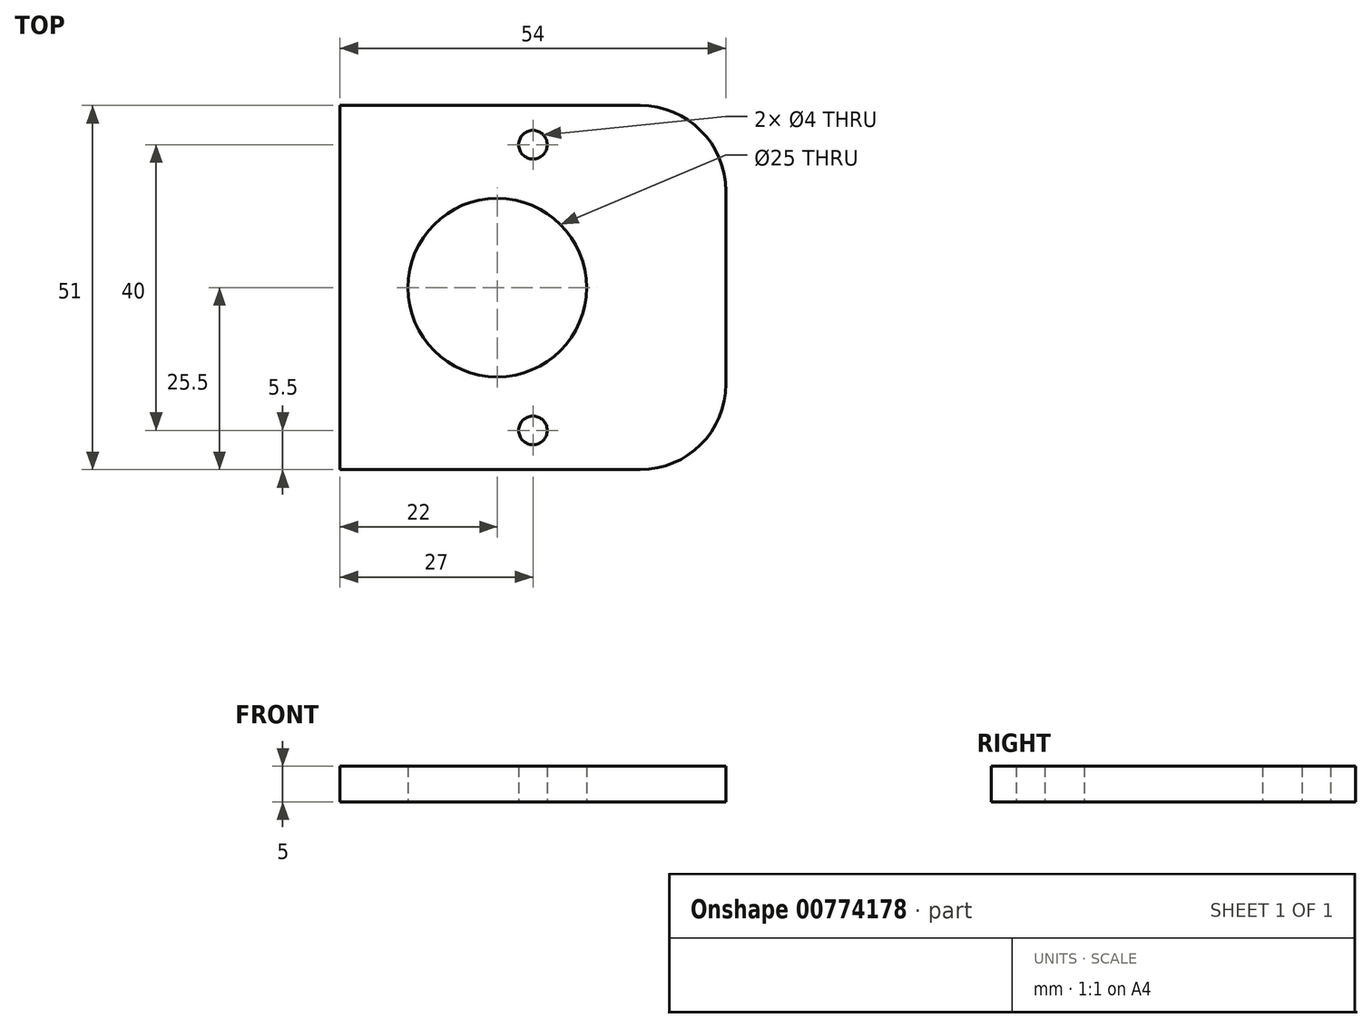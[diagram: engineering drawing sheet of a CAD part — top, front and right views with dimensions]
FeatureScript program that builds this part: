
annotation { "Feature Type Name" : "Feature", "Feature Type Description" : "" }
export const myFeature = defineFeature(function(context is Context, id is Id, definition is map)
    precondition{}
    {
        {
            var Q0;
            Q0=qCreatedBy(makeId("Top.planeOp"),FACE);
            var sketch = newSketch(context, id + "F0", { "sketchPlane" : qUnion([Q0])});
            skLineSegment(sketch, "E0.bottom", {"start": v(27, -25.5) * mm, "end": v(-27, -25.5) * mm});
            skLineSegment(sketch, "E0.top", {"start": v(27, 25.5) * mm, "end": v(-27, 25.5) * mm});
            skLineSegment(sketch, "E0.left", {"start": v(27, -25.5) * mm, "end": v(27, 25.5) * mm});
            skLineSegment(sketch, "E0.right", {"start": v(-27, -25.5) * mm, "end": v(-27, 25.5) * mm});
            skPoint(sketch, "E0.middle", {"position": v(0, 0) * mm});
            skLineSegment(sketch, "E1", {"start": v(0, 0) * mm, "end": v(-5, 0) * mm, "construction": true});
            skCircle(sketch, "E2", {"center": v(-5, 0) * mm, "radius": 12.5 * mm});
            skLineSegment(sketch, "E3", {"start": v(0, 0) * mm, "end": v(0, 20) * mm, "construction": true});
            skLineSegment(sketch, "E4", {"start": v(0, 0) * mm, "end": v(0, -20) * mm, "construction": true});
            skCircle(sketch, "E5", {"center": v(0, 20) * mm, "radius": 2 * mm});
            skCircle(sketch, "E6", {"center": v(0, -20) * mm, "radius": 2 * mm});
            skSolve(sketch);
        }
        {
            var Q0;
            Q0 = qSketchRegion(id + "F0", true);
            extrude(context, id + "F1", {"entities" : qUnion([Q0]), "depth" : 5 * mm, "offsetDistance" : 25 * mm});
        }
        {
            var Q0;
            Q0=makeQuery(id+"F1.opExtrude","SWEPT_EDGE",EDGE,{"disambiguationData":[OSD([sQuery(id+"F0.wireOp",EDGE,"E0.bottom"),sQuery(id+"F0.wireOp",EDGE,"E0.left")])]});
            var Q1;
            Q1=makeQuery(id+"F1.opExtrude","SWEPT_EDGE",EDGE,{"disambiguationData":[OSD([sQuery(id+"F0.wireOp",EDGE,"E0.top"),sQuery(id+"F0.wireOp",EDGE,"E0.left")])]});
            fillet(context, id + "F2", {"entities" : qUnion([Q0, Q1]), "radius" : 12 * mm, "tangentPropagation" : true, "allowEdgeOverflow" : false});
        }
    });
